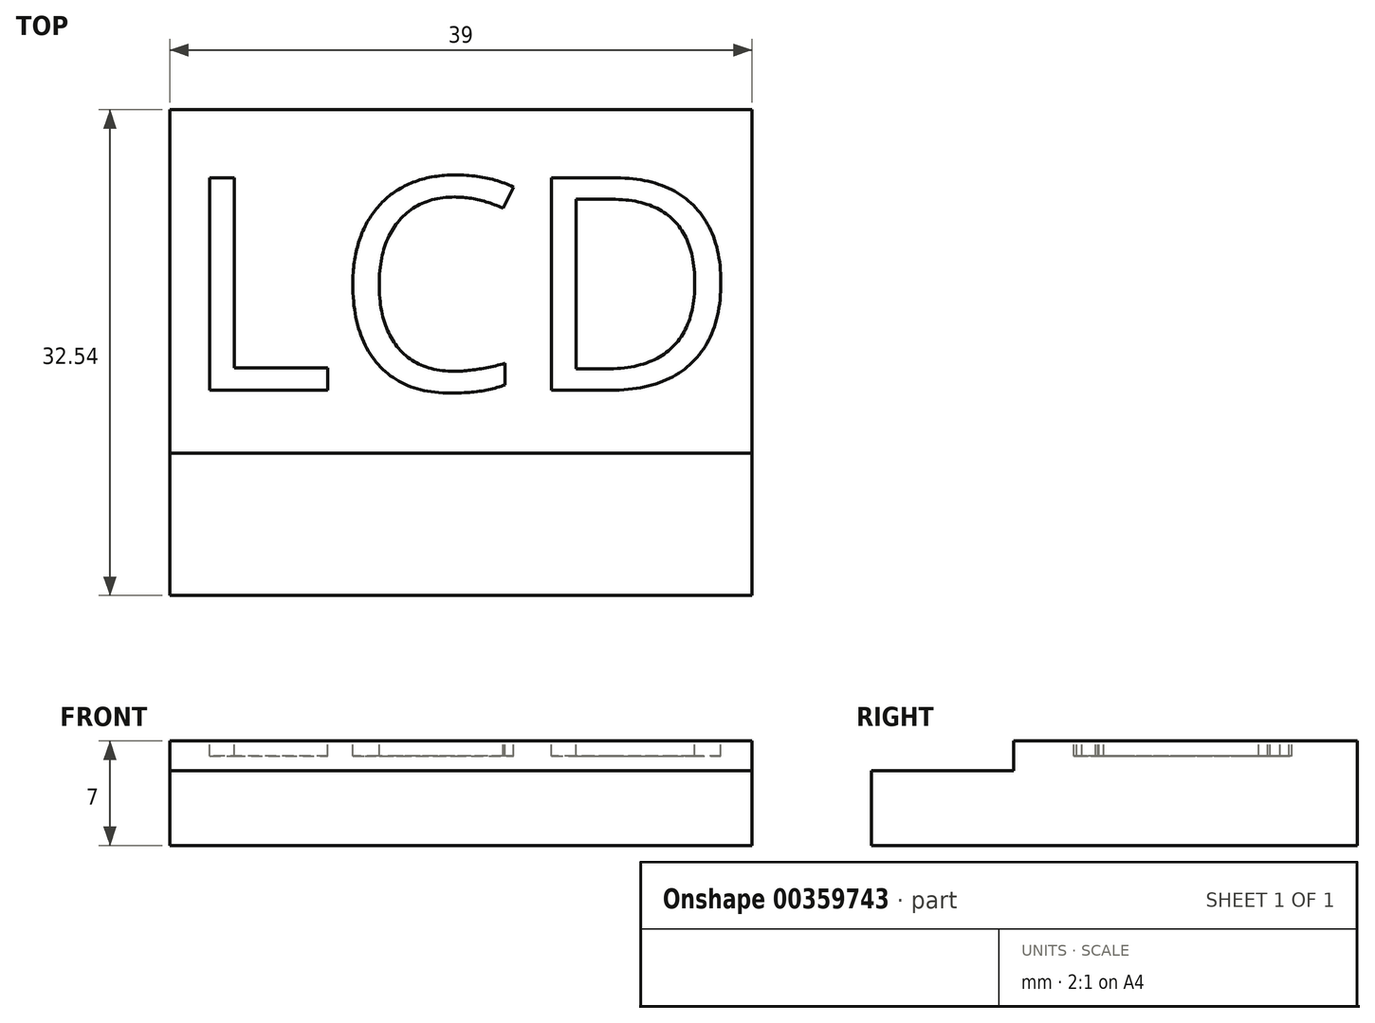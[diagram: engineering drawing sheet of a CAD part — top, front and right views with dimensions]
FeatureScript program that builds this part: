
annotation { "Feature Type Name" : "Feature", "Feature Type Description" : "" }
export const myFeature = defineFeature(function(context is Context, id is Id, definition is map)
    precondition{}
    {
        {
            var Q0;
            Q0=qCreatedBy(makeId("Top.planeOp"),FACE);
            var sketch = newSketch(context, id + "F0", { "sketchPlane" : qUnion([Q0])});
            skLineSegment(sketch, "E0.bottom", {"start": v(-8.52, 13.49) * mm, "end": v(30.48, 13.49) * mm});
            skLineSegment(sketch, "E0.top", {"start": v(-8.52, -19.05) * mm, "end": v(30.48, -19.05) * mm});
            skLineSegment(sketch, "E0.left", {"start": v(-8.52, 13.49) * mm, "end": v(-8.52, -19.05) * mm});
            skLineSegment(sketch, "E0.right", {"start": v(30.48, 13.49) * mm, "end": v(30.48, -19.05) * mm});
            skLineSegment(sketch, "E1", {"start": v(-8.52, -9.51) * mm, "end": v(30.48, -9.51) * mm});
            skSolve(sketch);
        }
        {
            var Q0;
            {var subQ0=sQuery(id+"F0.wireOp",EDGE,"E0.top");Q0=makeQuery(id+"F0.imprint","IMPRINT",FACE,{"disambiguationData":[TD([[makeQuery(id+"F0.imprint","IMPRINT",EDGE,{"derivedFrom":subQ0}),1.0]])]});}
            var Q1;
            {var subQ0=sQuery(id+"F0.wireOp",EDGE,"E0.bottom");Q1=makeQuery(id+"F0.imprint","IMPRINT",FACE,{"disambiguationData":[TD([[makeQuery(id+"F0.imprint","IMPRINT",EDGE,{"derivedFrom":subQ0}),-1.0]])]});}
            extrude(context, id + "F1", {"entities" : qUnion([Q0, Q1]), "depth" : 5 * mm});
        }
        {
            var Q0;
            Q0=makeQuery(id+"F1.opExtrude","CAP_FACE",FACE,{"disambiguationData":[OSD([sQuery(id+"F0.wireOp",EDGE,"E0.bottom"),sQuery(id+"F0.wireOp",EDGE,"E0.top"),sQuery(id+"F0.wireOp",EDGE,"E0.left"),sQuery(id+"F0.wireOp",EDGE,"E0.right")])],"isStart":false});
            var sketch = newSketch(context, id + "F2", { "sketchPlane" : qUnion([Q0])});
            skLineSegment(sketch, "E2", {"start": v(-8.52, -9.51) * mm, "end": v(30.48, -9.51) * mm});
            skLineSegment(sketch, "E3.0", {"start": v(-8.52, 13.49) * mm, "end": v(30.48, 13.49) * mm});
            skLineSegment(sketch, "E3.1", {"start": v(-8.52, 13.49) * mm, "end": v(-8.52, -9.51) * mm});
            skLineSegment(sketch, "E3.2", {"start": v(30.48, 13.49) * mm, "end": v(30.48, -9.51) * mm});
            skPoint(sketch, "E4.orphan", {"position": v(-8.52, -19.05) * mm});
            skPoint(sketch, "E5.orphan", {"position": v(30.48, -19.05) * mm});
            skSolve(sketch);
        }
        {
            var Q0;
            Q0=makeQuery(id+"F2.imprint","IMPRINT",FACE,{"disambiguationData":[TD([[makeQuery(id+"F2.imprint","IMPRINT",EDGE,{"derivedFrom":sQuery(id+"F2.wireOp",EDGE,"E2")}),1.0]])]});
            extrude(context, id + "F3", {"entities" : qUnion([Q0]), "operationType" : NewBodyOperationType.ADD, "depth" : 2 * mm});
        }
        {
            var Q0;
            Q0=makeQuery(id+"F3.opExtrude","CAP_FACE",FACE,{"disambiguationData":[OSD([sQuery(id+"F2.wireOp",EDGE,"E2"),sQuery(id+"F2.wireOp",EDGE,"E3.0"),sQuery(id+"F2.wireOp",EDGE,"E3.1"),sQuery(id+"F2.wireOp",EDGE,"E3.2")])],"isStart":false});
            var sketch = newSketch(context, id + "F4", { "sketchPlane" : qUnion([Q0])});
            skText(sketch, "E6", { "text": "LCD", "fontName": "OpenSans-Regular.ttf"});
            const initialGuessF4  = {"E6": [-0.00781, -0.0053, 1, 0, 0.01434]};
            skSetInitialGuess(sketch, initialGuessF4);
            skSolve(sketch);
        }
        {
            var Q0;
            Q0=makeQuery(id+"F4.imprint","IMPRINT",FACE,{"disambiguationData":[TD([[makeQuery(id+"F4.imprint","IMPRINT",EDGE,{"derivedFrom":sQuery(id+"F4.wireOp",EDGE,"E6.sketch_text.stroke-0")}),-1.0]])]});
            var Q1;
            Q1=makeQuery(id+"F4.imprint","IMPRINT",FACE,{"disambiguationData":[TD([[makeQuery(id+"F4.imprint","IMPRINT",EDGE,{"derivedFrom":sQuery(id+"F4.wireOp",EDGE,"E6.sketch_text.stroke-6")}),-1.0]])]});
            var Q2;
            Q2=makeQuery(id+"F4.imprint","IMPRINT",FACE,{"disambiguationData":[TD([[makeQuery(id+"F4.imprint","IMPRINT",EDGE,{"derivedFrom":sQuery(id+"F4.wireOp",EDGE,"E6.sketch_text.stroke-21")}),-1.0]])]});
            extrude(context, id + "F5", {"entities" : qUnion([Q0, Q1, Q2]), "operationType" : NewBodyOperationType.REMOVE, "oppositeDirection" : true, "depth" : 1 * mm});
        }
    });
